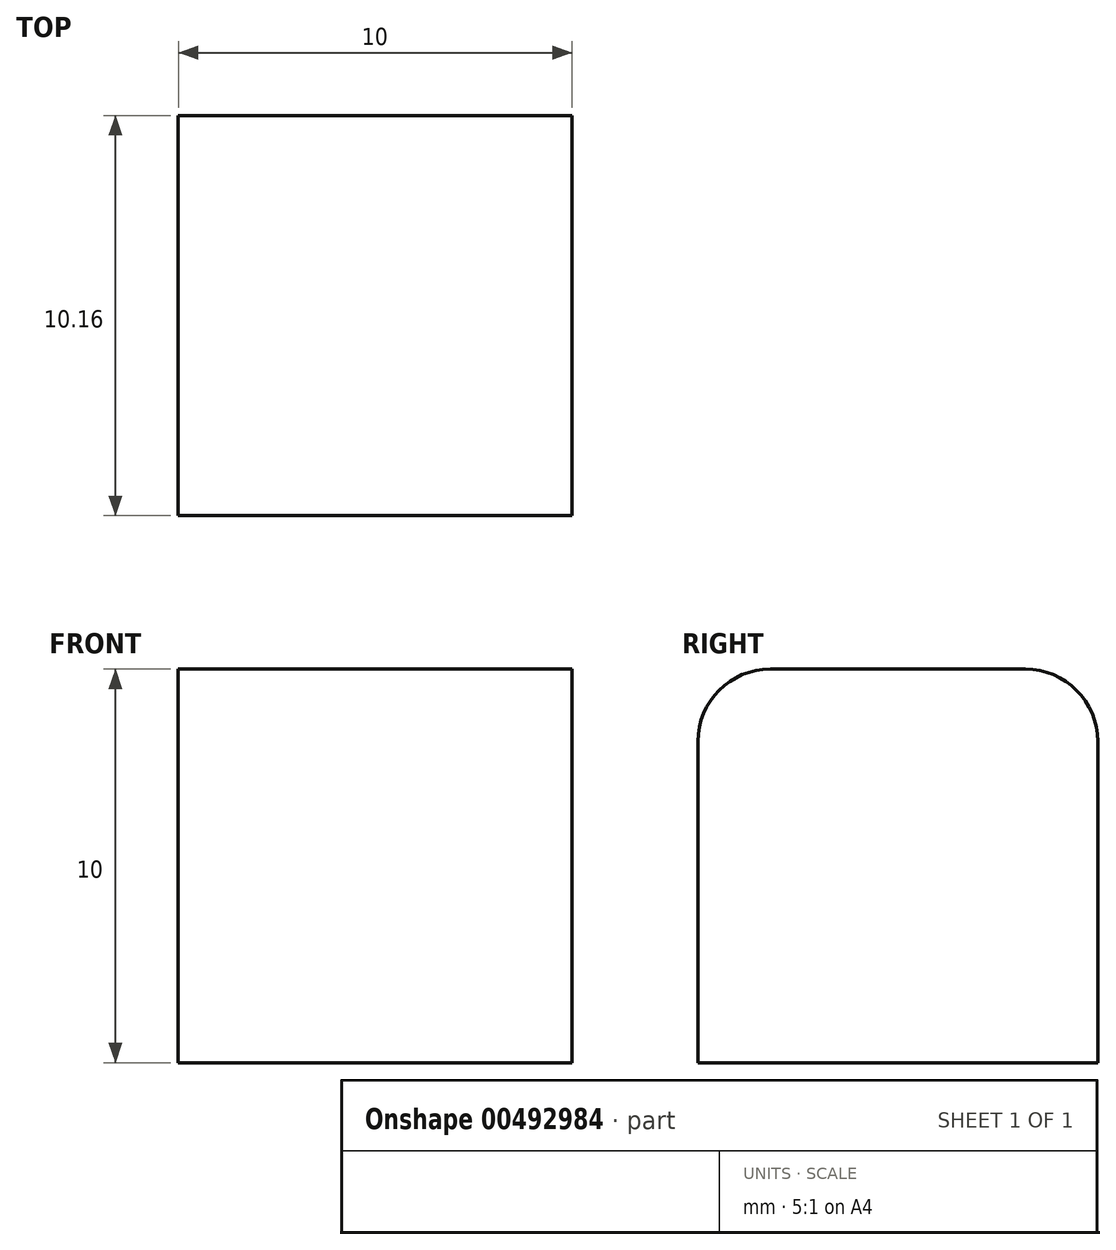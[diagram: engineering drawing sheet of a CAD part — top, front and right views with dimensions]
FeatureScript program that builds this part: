
annotation { "Feature Type Name" : "Feature", "Feature Type Description" : "" }
export const myFeature = defineFeature(function(context is Context, id is Id, definition is map)
    precondition{}
    {
        {
            var Q0;
            Q0=qCreatedBy(makeId("Front.planeOp"),FACE);
            var sketch = newSketch(context, id + "F0", { "sketchPlane" : qUnion([Q0])});
            skLineSegment(sketch, "E0.bottom", {"start": v(-12.6, 8.04) * mm, "end": v(-22.6, 8.04) * mm});
            skLineSegment(sketch, "E0.top", {"start": v(-12.6, 18.04) * mm, "end": v(-22.6, 18.04) * mm});
            skLineSegment(sketch, "E0.left", {"start": v(-12.6, 8.04) * mm, "end": v(-12.6, 18.04) * mm});
            skLineSegment(sketch, "E0.right", {"start": v(-22.6, 8.04) * mm, "end": v(-22.6, 18.04) * mm});
            skPoint(sketch, "E0.middle", {"position": v(-17.6, 13.04) * mm});
            skSolve(sketch);
        }
        {
            var Q0;
            Q0=makeQuery(id+"F0.imprint","IMPRINT",FACE,{"disambiguationData":[TD([[makeQuery(id+"F0.imprint","IMPRINT",EDGE,{"derivedFrom":sQuery(id+"F0.wireOp",EDGE,"E0.bottom")}),-1.0]])]});
            extrude(context, id + "F1", {"entities" : qUnion([Q0]), "depth" : 10.16 * mm});
        }
        {
            var Q0;
            Q0=makeQuery(id+"F1.opExtrude","CAP_EDGE",EDGE,{"disambiguationData":[OSD([sQuery(id+"F0.wireOp",EDGE,"E0.top")])],"isStart":false});
            fillet(context, id + "F2", {"entities" : qUnion([Q0]), "radius" : 1.84 * mm, "tangentPropagation" : true, "allowEdgeOverflow" : false});
        }
        {
            var Q0;
            Q0=makeQuery(id+"F1.opExtrude","CAP_EDGE",EDGE,{"disambiguationData":[OSD([sQuery(id+"F0.wireOp",EDGE,"E0.top")])],"isStart":true});
            fillet(context, id + "F3", {"entities" : qUnion([Q0]), "radius" : 1.84 * mm, "tangentPropagation" : true, "allowEdgeOverflow" : false});
        }
    });
